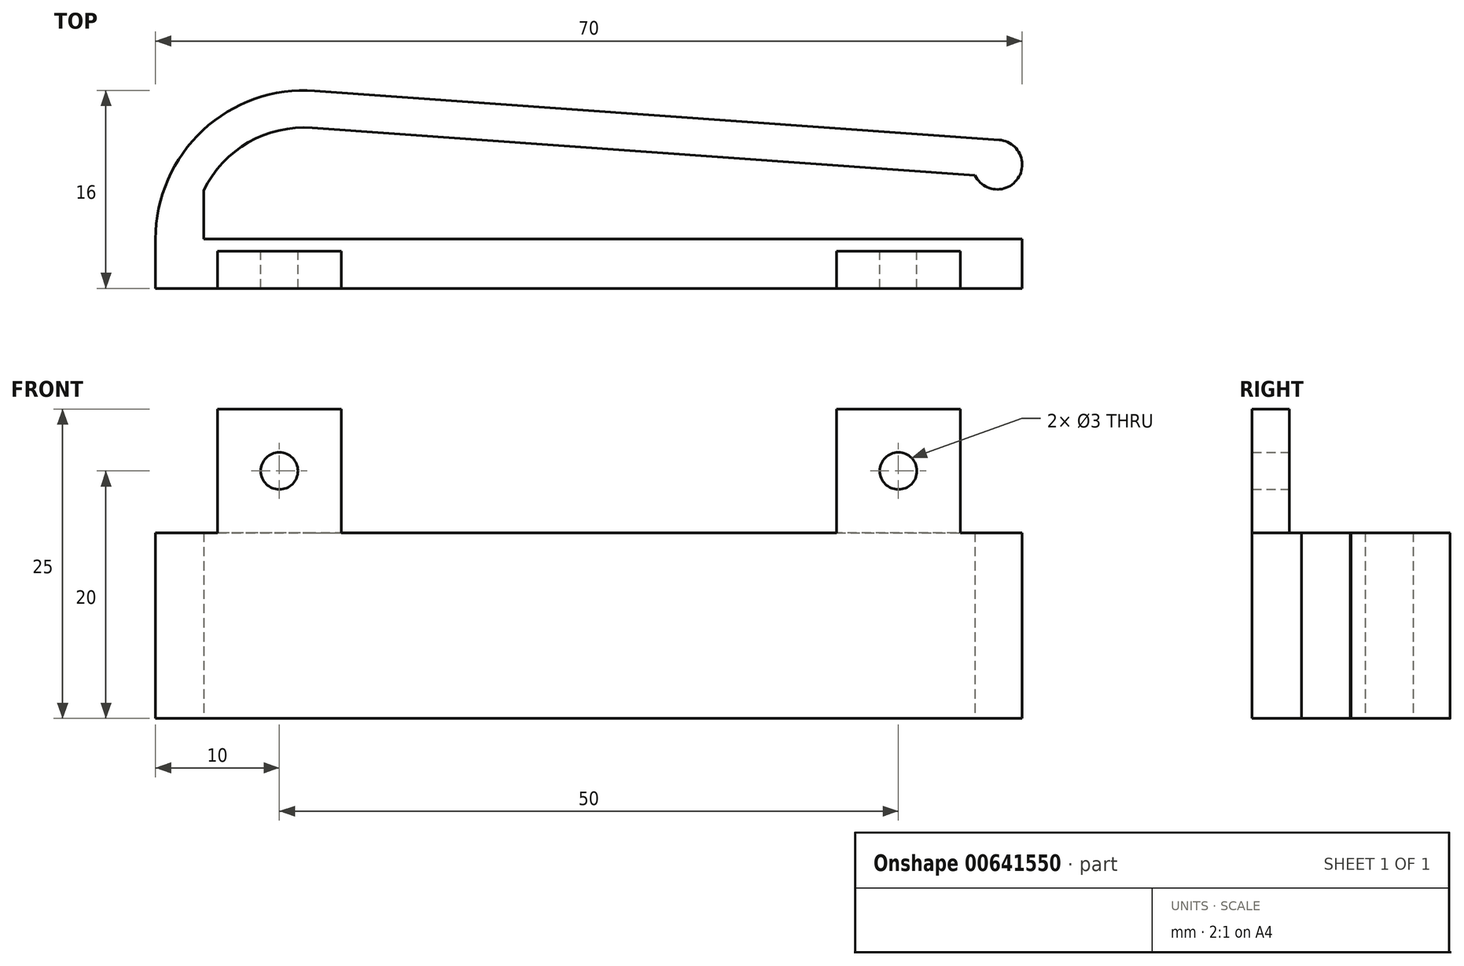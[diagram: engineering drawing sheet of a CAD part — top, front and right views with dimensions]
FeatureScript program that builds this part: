
annotation { "Feature Type Name" : "Feature", "Feature Type Description" : "" }
export const myFeature = defineFeature(function(context is Context, id is Id, definition is map)
    precondition{}
    {
        {
            var Q0;
            Q0=qCreatedBy(makeId("Top.planeOp"),FACE);
            var sketch = newSketch(context, id + "F0", { "sketchPlane" : qUnion([Q0])});
            skLineSegment(sketch, "E0.bottom", {"start": v(0, 0) * mm, "end": v(70, 0) * mm});
            skLineSegment(sketch, "E0.top", {"start": v(3.9, 4) * mm, "end": v(70, 4) * mm});
            skLineSegment(sketch, "E0.left", {"start": v(0, 0) * mm, "end": v(0, 4) * mm});
            skLineSegment(sketch, "E0.right", {"start": v(70, 0) * mm, "end": v(70, 4) * mm});
            skLineSegment(sketch, "E1", {"start": v(3.9, 4) * mm, "end": v(12, 4) * mm, "construction": true});
            skArc(sketch, "E2", {"start": v(12.86, 15.97) * mm, "mid": v(3.82, 12.78) * mm, "end": v(0, 4) * mm});
            skArc(sketch, "E3.0", {"start": v(12.65, 12.98) * mm, "mid": v(7.5, 11.8) * mm, "end": v(3.9, 7.92) * mm});
            skLineSegment(sketch, "E4", {"start": v(3.9, 4) * mm, "end": v(3.9, 7.92) * mm});
            skLineSegment(sketch, "E5", {"start": v(70, 4) * mm, "end": v(68, 4) * mm, "construction": true});
            skLineSegment(sketch, "E6", {"start": v(68, 4) * mm, "end": v(68, 10) * mm, "construction": true});
            skArc(sketch, "E7", {"start": v(66.2, 9.13) * mm, "mid": v(69.66, 8.88) * mm, "end": v(68.14, 12) * mm});
            skLineSegment(sketch, "E8", {"start": v(68.14, 12) * mm, "end": v(12.86, 15.97) * mm});
            skLineSegment(sketch, "E9", {"start": v(12.65, 12.98) * mm, "end": v(66.2, 9.13) * mm});
            skLineSegment(sketch, "E10", {"start": v(0, 0) * mm, "end": v(5, 0) * mm, "construction": true});
            skLineSegment(sketch, "E11", {"start": v(70, 0) * mm, "end": v(65, 0) * mm, "construction": true});
            skLineSegment(sketch, "E12.bottom", {"start": v(5, 0) * mm, "end": v(15, 0) * mm});
            skLineSegment(sketch, "E12.top", {"start": v(5, 3) * mm, "end": v(15, 3) * mm});
            skLineSegment(sketch, "E12.left", {"start": v(5, 0) * mm, "end": v(5, 3) * mm});
            skLineSegment(sketch, "E12.right", {"start": v(15, 0) * mm, "end": v(15, 3) * mm});
            skLineSegment(sketch, "E13.bottom", {"start": v(65, 0) * mm, "end": v(55, 0) * mm});
            skLineSegment(sketch, "E13.top", {"start": v(65, 3) * mm, "end": v(55, 3) * mm});
            skLineSegment(sketch, "E13.left", {"start": v(65, 0) * mm, "end": v(65, 3) * mm});
            skLineSegment(sketch, "E13.right", {"start": v(55, 0) * mm, "end": v(55, 3) * mm});
            skSolve(sketch);
        }
        {
            var Q0;
            Q0=makeQuery(id+"F0.imprint","IMPRINT",FACE,{"disambiguationData":[TD([[makeQuery(id+"F0.imprint","IMPRINT",EDGE,{"derivedFrom":sQuery(id+"F0.wireOp",EDGE,"E0.top")}),-1.0]])]});
            extrude(context, id + "F1", {"entities" : qUnion([Q0]), "depth" : 15 * mm, "offsetDistance" : 25 * mm});
        }
        {
            var Q0;
            Q0=makeQuery(id+"F0.imprint","IMPRINT",FACE,{"disambiguationData":[TD([[makeQuery(id+"F0.imprint","IMPRINT",EDGE,{"derivedFrom":sQuery(id+"F0.wireOp",EDGE,"E12.top")}),-1.0]])]});
            var Q1;
            Q1=makeQuery(id+"F0.imprint","IMPRINT",FACE,{"disambiguationData":[TD([[makeQuery(id+"F0.imprint","IMPRINT",EDGE,{"derivedFrom":sQuery(id+"F0.wireOp",EDGE,"E13.top")}),1.0]])]});
            extrude(context, id + "F2", {"entities" : qUnion([Q0, Q1]), "operationType" : NewBodyOperationType.ADD, "depth" : 25 * mm, "offsetDistance" : 25 * mm});
        }
        {
            var Q0;
            Q0=makeQuery(id+"F2.opExtrude","SWEPT_FACE",FACE,{"disambiguationData":[OSD([sQuery(id+"F0.wireOp",EDGE,"E12.top")])]});
            var sketch = newSketch(context, id + "F3", { "sketchPlane" : qUnion([Q0])});
            skLineSegment(sketch, "E14", {"start": v(-10, 15) * mm, "end": v(-10, 25) * mm, "construction": true});
            skCircle(sketch, "E15", {"center": v(-10, 20) * mm, "radius": 1.5 * mm});
            skSolve(sketch);
        }
        {
            var Q0;
            Q0=makeQuery(id+"F2.opExtrude","SWEPT_FACE",FACE,{"disambiguationData":[OSD([sQuery(id+"F0.wireOp",EDGE,"E13.top")])]});
            var sketch = newSketch(context, id + "F4", { "sketchPlane" : qUnion([Q0])});
            skLineSegment(sketch, "E16", {"start": v(-60, 15) * mm, "end": v(-60, 25) * mm, "construction": true});
            skCircle(sketch, "E17", {"center": v(-60, 20) * mm, "radius": 1.5 * mm});
            skSolve(sketch);
        }
        {
            var Q0;
            Q0=makeQuery(id+"F4.imprint","IMPRINT",FACE,{"disambiguationData":[TD([[makeQuery(id+"F4.imprint","IMPRINT",EDGE,{"derivedFrom":sQuery(id+"F4.wireOp",EDGE,"E17")}),1.0]])]});
            var Q1;
            Q1=makeQuery(id+"F3.imprint","IMPRINT",FACE,{"disambiguationData":[TD([[makeQuery(id+"F3.imprint","IMPRINT",EDGE,{"derivedFrom":sQuery(id+"F3.wireOp",EDGE,"E15")}),1.0]])]});
            extrude(context, id + "F5", {"entities" : qUnion([Q0, Q1]), "operationType" : NewBodyOperationType.REMOVE, "oppositeDirection" : true, "depth" : 5 * mm, "offsetDistance" : 25 * mm});
        }
    });
